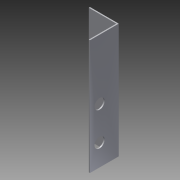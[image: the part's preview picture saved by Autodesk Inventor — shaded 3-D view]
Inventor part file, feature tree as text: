
AUTODESK INVENTOR PART (.ipt)
format: ipt  version: 2014 SP1 (Build 180222100, 222)  size: 99,840 bytes
history: native  units: in
note: dims shown in document units (in); Inventor stores cm internally (conversion verified against a paired STEP export)
features: extrude x3, sketch x3
ambient origin geometry x8: Origin, YZ Plane, XZ Plane, XY Plane, X Axis, Y Axis, Z Axis, Center Point
bodies: Solid1 (feature_tree)
feature tree (6):
  extrude  "Extrusion1"  Depth=0.0312in
  extrude  "Extrusion2"  Depth=3.0in
  extrude  "Extrusion3"  Depth=3.0in TaperAngle=0.0deg
  sketch  "Sketch1"  dims[d0=0.75in d1=0.0312in]
  sketch  "Sketch2"  dims[d2=3.0in d3=0.0in d4=0.875in]
  sketch  "Sketch3"  dims[d5=0.266in d7=3.0in d8=0.0in d9=0.15in d10=0.8543in d11=0.4055in d12=0.75in d13=0.25in d14=3.0in d15=0.0in d16=0.5in d17=0.5625in]
